# Revit family: Leuchtenträger-Systeme_Aufhängebügel
name_source: partatom
category: Generic Models
revit_build: Autodesk Revit 2015 (Build: 20140606_1530(x64)
units: mm (PartAtom-declared; Revit-internal decimal feet)

## types (2) — shared parameters
Manufacturer = OBO Bettermann
Material = Steel, Galvanized
URL = http://www.obo-bettermann.com

## per-type parameters (varying)
| type | Diameter dimesion | GTIN | Lenght | Manufacturer Art. No. | Width |
| AHB 100 D5 FT | 5 mm  [stored 0.0164042 ft] | 4012195834878 | 12 mm  [stored 0.0393701 ft] | 6066510 | 110 mm  [stored 0.360892 ft] |
| AHB 50 D4 FT | 4 mm  [stored 0.0131234 ft] | 4012196935895 | 8 mm  [stored 0.0262467 ft] | 6066505 | 59 mm |

note: column(s) folded — value = type name in every type: Article Type

note: [stored X ft] marks values corroborated as IEEE doubles in the binary element streams (Revit-internal decimal feet)

## geometry (parser evidence)
native form markers: Sweep x2
no freeform markers — native parametric forms only
